# Revit family: reyq22t
name_source: partatom
category: Mechanical Equipment
revit_build: Autodesk Revit 2017 (Build: 20170816_0615(x64)
units: mm (PartAtom-declared; Revit-internal decimal feet)

## family parameters
Cut with Voids When Loaded = No
Host = Face
OmniClass Number = 23.75.10.21.14
OmniClass Title = Rooftop Heat Pumps
Part Type = Normal
Room Calculation Point = No
Round Connector Dimension = Use Diameter
Shared = No

## types (1)
- reyq22t
    COP at max. capacity 6°CWB kW/kW = 4.10 kW/kW
    COP at maximum capacity kW = 0
    COP at nom. capacity 6°CWB kW/kW = 4.29 kW/kW
    COP at nom. capacity Eurovent kW/kW = 0
    COP at nominal capacity kW = 0
    Capacity range HP = 22 HP
    Continuous heating = v
    Cooling capacity Nom. 35°CDB kW = 61.5 (1) kW
    Cooling capacity Nom. Eurovent kW = 0
    Cooling capacity Nom. kW = 0
    Current - 50Hz Maximum fuse amps (MFA) A = 50 A
    Default Elevation = 1000 mm  [stored 3.28084 ft]
    Description = Air cooled - heat recovery
    Dimensions Unit Height/Width/Depth mm = -/-/-
    EER at nom. capacity 35°CDB kW/kW = 3.75 kW/kW
    EER at nom. capacity Eurovent kW/kW = 0
    ESEER - Automatic = 07.lip
    ESEER - Standard = maj.54
    Fan Discharge direction = 0
    Fan External static pressure Max. Pa = 0
    Fan External static pressure Nom. Pa = 0
    Fan Type = 0
    Heating capacity Max. 6°CWB kW = 69.0 (2) kW
    Heating capacity Max. kW = 0
    Heating capacity Nom. 6°CWB kW = 61.5 (2) kW
    Heating capacity Nom. Eurovent kW = 0
    Heating capacity Nom. kW = 0
    IfcExportAs = IfcUnitaryEquipmentType
    IfcExportType = ROOFTOPUNIT
    Indoor index connection Max. = 715
    Indoor index connection Min. = 275
    Indoor index connection Nom. = 550
    Installation Manual = http://www.daikineurope.com
    Manufacturer = Daikin Europe N.V.
    Maximum number of connectable indoor units = 64 (5)
    Model = VRV IV
    Operation range Cooling Min./Max. °CDB = -5.0/43.0 °CDB
    Operation range Heating Min./Max. °CWB = -20/15.5 °CWB
    Operation range Inlet water temperature Cooling Min./Max. °CDB = -/-
    Operation range Inlet water temperature Heating Min./Max. °CWB = -/-
    Piping connections Between Compressor module (CM) and heat exchanger module (HM) Gas OD mm = 0
    Piping connections Between Compressor module (CM) and heat exchanger module (HM) Liquid OD mm = 0
    Piping connections Between Compressor module (CM) and indoor units (IU) Gas OD mm = 0
    Piping connections Between Compressor module (CM) and indoor units (IU) Liquid OD mm = 0
    Piping connections Discharge gas OD mm = 28.6 mm
    Piping connections Gas OD mm = 28.6 mm
    Piping connections Liquid OD mm = 15.9 mm
    Piping connections Oil equalizing OD mm = 0
    Piping connections Total piping length System Actual m = 1,000 (9) m
    Power input - 50Hz Cooling Nom. 35°CDB kW = 16,38 kW
    Power input - 50Hz Cooling Nom. Eurovent kW = 0
    Power input - 50Hz Heating Max. 6°CWB kW = 16,81 kW
    Power input - 50Hz Heating Nom. 6°CWB kW = 14,34 kW
    Power input - 50Hz Heating Nom. Eurovent kW = 0
    Power supply Phase/Frequency/Voltage = 3N~/50/380-415 V
    RSen_C_IFC_version = 2x3
    RSen_C_code_ETIM = Air-conditioning split system – multi-split condensing unit, air-cooled
    RSen_C_code_ETIM_URL = https://prod.etim-international.com
    RSen_C_code_article = REYQ22T7Y1B
    RSen_C_code_product = REYQ22T
    RSen_C_code_product_class = REYQ-T
    RSen_C_content_date_changed = 13/01/2017
    RSen_C_content_date_issue = 13/01/2017
    RSen_C_content_provider = Daikin Europe N.V.
    RSen_C_content_version = v1.0
    RSen_C_description = Air cooled - heat recovery
    RSen_C_diameter_type = OD
    RSen_C_diameter_type_index = 1
    RSen_C_license = Creative Commons Attribution NoDerivs (CC-ND)
    RSen_C_license_info = https://tldrlegal.com
    RSen_C_material = RSen_x_rgb 202 196 176 T00 silk gray_gen
    RSen_C_model = VRV IV
    RSen_C_revit_version = 2015
    RSen_C_type = VRV IV heat recovery
    RSen_C_type_comments = Outdoor unit
    RSen_E_c01_apparent_power = 16810 VA
    RSen_E_c01_apparent_power_phase_1 = 5603 VA
    RSen_E_c01_apparent_power_phase_2 = 5603 VA
    RSen_E_c01_apparent_power_phase_3 = 5603 VA
    RSen_E_c01_current = 0 A
    RSen_E_c01_description = c01_el
    RSen_E_c01_division_engine = No
    RSen_E_c01_load_class = Other
    RSen_E_c01_number_of_poles = 3
    RSen_E_c01_power = 16810 W
    RSen_E_c01_power_factor = 1
    RSen_E_c01_power_factor_state = Lagging
    RSen_E_c01_system_type = Power - Unbalanced
    RSen_E_c01_voltage = 400 V
    RSen_E_c01_yes_no = Yes
    RSen_E_c02_description = c02_controls
    RSen_E_c02_yes_no = Yes
    RSen_P_c01_description = c01_liquid pipe
    RSen_P_c01_diameter = 16 mm  [stored 0.0524934 ft]
    RSen_P_c01_diameter_calc = 16 mm  [stored 0.0524934 ft]
    RSen_P_c01_flow_configuration = Calculated
    RSen_P_c01_flow_direction = Out
    RSen_P_c01_loss_method = Not Defined
    RSen_P_c01_system_classification = Hydronic Supply
    RSen_P_c01_yes_no = Yes
    RSen_P_c02_description = c02_gas pipe
    RSen_P_c02_diameter = 29 mm
    RSen_P_c02_diameter_calc = 29 mm
    RSen_P_c02_flow_configuration = Calculated
    RSen_P_c02_flow_direction = In
    RSen_P_c02_loss_method = Not Defined
    RSen_P_c02_system_classification = Hydronic Return
    RSen_P_c02_yes_no = Yes
    RSen_P_c03_description = c03_equalising pipe
    RSen_P_c03_diameter = 29 mm
    RSen_P_c03_diameter_calc = 29 mm
    RSen_P_c03_flow_configuration = Calculated
    RSen_P_c03_flow_direction = Bidirectional
    RSen_P_c03_loss_method = Not Defined
    RSen_P_c03_system_classification = Global
    RSen_P_c03_yes_no = Yes
    Refrigerant Charge TCO2Eq = 0
    Refrigerant Charge kg = 0
    Refrigerant GWP = 0
    Refrigerant Type = 0
    Sound power level Cooling Nom. dBA = 0
    Sound pressure level Cooling Nom. dBA = 0
    Specification Text = https://my.daikin.eu
    System Compressor unit = 0
    System Function unit = 0
    System Heat exchanger unit = 0
    System Outdoor unit module 1 = REYQ10T
    System Outdoor unit module 2 = REYQ12T
    System Outdoor unit module 3 = 0
    System Outdoor unit module 4 = 0
    TBQ_I BaseKeynote = 58.10
    TBQ_I Spacing_default = 200 mm  [stored 0.656168 ft]
    TBQ_I Spacing_minimum = 20 mm  [stored 0.0656168 ft]
    Type Comments = Outdoor unit
    URL = www.daikineurope.com
    Weight Unit kg = 0
    ZZZ_Clearance behind unit_Length = 600 mm  [stored 1.9685 ft]
    ZZZ_Clearance zone_back_Length = 300 mm  [stored 0.984252 ft]
    ZZZ_Clearance zone_bottom_Length = 0 mm  [stored 0 ft]
    ZZZ_Clearance zone_front_Length = 500 mm  [stored 1.64042 ft]
    ZZZ_Clearance zone_left_Length = 10 mm  [stored 0.0328084 ft]
    ZZZ_Clearance zone_material_Material = RSen_x_rgb 255 128 128 T80 red_gen
    ZZZ_Clearance zone_right_Length = 10 mm  [stored 0.0328084 ft]
    ZZZ_Clearance zone_top_Length = 0 mm  [stored 0 ft]
    ZZZ_Component_01_LOD400_FamilyType_Mechanical Equipment = GEO_none_daikin : standard
    ZZZ_Component_01_Y_Length = 0 mm  [stored 0 ft]
    ZZZ_Component_01_Z_Length = 0 mm  [stored 0 ft]
    ZZZ_Component_01_description_Text = REYQ10T
    ZZZ_Component_01_fan_X_Length = 30 mm  [stored 0.0984252 ft]
    ZZZ_Component_01_fan_Y_Length = 0 mm  [stored 0 ft]
    ZZZ_Component_01_fan_Z_Length = 0 mm  [stored 0 ft]
    ZZZ_Component_01_fan_height_Length = 3 mm  [stored 0.00984252 ft]
    ZZZ_Component_01_fan_length_Length = 830 mm  [stored 2.7231 ft]
    ZZZ_Component_01_fan_material_Material = RSen_x_rgb 189 187 185 T80 gray_gen
    ZZZ_Component_01_fan_plane_Integer = 1
    ZZZ_Component_01_fan_width_Length = 725 mm  [stored 2.37861 ft]
    ZZZ_Component_01_height_Length = 1685 mm  [stored 5.52822 ft]
    ZZZ_Component_01_length_Length = 930 mm  [stored 3.05118 ft]
    ZZZ_Component_01_material_Material = RSen_x_rgb 202 196 176 T00 silk gray_gen
    ZZZ_Component_01_width_Length = 765 mm  [stored 2.50984 ft]
    ZZZ_Component_02_LOD400_FamilyType_Mechanical Equipment = GEO_none_daikin : standard
    ZZZ_Component_02_Y_Length = 0 mm  [stored 0 ft]
    ZZZ_Component_02_Z_Length = 0 mm  [stored 0 ft]
    ZZZ_Component_02_description_Text = REYQ12T
    ZZZ_Component_02_fan_X_Length = 30 mm  [stored 0.0984252 ft]
    ZZZ_Component_02_fan_Y_Length = 0 mm  [stored 0 ft]
    ZZZ_Component_02_fan_Z_Length = 0 mm  [stored 0 ft]
    ZZZ_Component_02_fan_height_Length = 3 mm  [stored 0.00984252 ft]
    ZZZ_Component_02_fan_length_Length = 830 mm  [stored 2.7231 ft]
    ZZZ_Component_02_fan_material_Material = RSen_x_rgb 189 187 185 T80 gray_gen
    ZZZ_Component_02_fan_plane_Integer = 1
    ZZZ_Component_02_fan_width_Length = 725 mm  [stored 2.37861 ft]
    ZZZ_Component_02_height_Length = 1685 mm  [stored 5.52822 ft]
    ZZZ_Component_02_length_Length = 930 mm  [stored 3.05118 ft]
    ZZZ_Component_02_material_Material = RSen_x_rgb 202 196 176 T00 silk gray_gen
    ZZZ_Component_02_width_Length = 765 mm  [stored 2.50984 ft]
    ZZZ_Component_03_LOD400_FamilyType_Mechanical Equipment = GEO_none_daikin : standard
    ZZZ_Component_03_Y_Length = 0 mm  [stored 0 ft]
    ZZZ_Component_03_Z_Length = 0 mm  [stored 0 ft]
    ZZZ_Component_03_description_Text = -
    ZZZ_Component_03_fan_X_Length = 0 mm  [stored 0 ft]
    ZZZ_Component_03_fan_Y_Length = 0 mm  [stored 0 ft]
    ZZZ_Component_03_fan_Z_Length = 0 mm  [stored 0 ft]
    ZZZ_Component_03_fan_height_Length = 0 mm  [stored 0 ft]
    ZZZ_Component_03_fan_length_Length = 0 mm  [stored 0 ft]
    ZZZ_Component_03_fan_material_Material = RSen_x_rgb 189 187 185 T80 gray_gen
    ZZZ_Component_03_fan_plane_Integer = 1
    ZZZ_Component_03_fan_width_Length = 0 mm  [stored 0 ft]
    ZZZ_Component_03_height_Length = 0 mm  [stored 0 ft]
    ZZZ_Component_03_length_Length = 0 mm  [stored 0 ft]
    ZZZ_Component_03_material_Material = RSen_x_rgb 202 196 176 T00 silk gray_gen
    ZZZ_Component_03_width_Length = 0 mm  [stored 0 ft]
    ZZZ_Component_04_LOD400_FamilyType_Mechanical Equipment = GEO_none_daikin : standard
    ZZZ_Component_04_Y_Length = 0 mm  [stored 0 ft]
    ZZZ_Component_04_Z_Length = 0 mm  [stored 0 ft]
    ZZZ_Component_04_description_Text = -
    ZZZ_Component_04_fan_X_Length = 0 mm  [stored 0 ft]
    ZZZ_Component_04_fan_Y_Length = 0 mm  [stored 0 ft]
    ZZZ_Component_04_fan_Z_Length = 0 mm  [stored 0 ft]
    ZZZ_Component_04_fan_height_Length = 0 mm  [stored 0 ft]
    ZZZ_Component_04_fan_length_Length = 0 mm  [stored 0 ft]
    ZZZ_Component_04_fan_material_Material = <By Category>
    ZZZ_Component_04_fan_plane_Integer = 1
    ZZZ_Component_04_fan_width_Length = 0 mm  [stored 0 ft]
    ZZZ_Component_04_height_Length = 0 mm  [stored 0 ft]
    ZZZ_Component_04_length_Length = 0 mm  [stored 0 ft]
    ZZZ_Component_04_material_Material = <By Category>
    ZZZ_Component_04_width_Length = 0 mm  [stored 0 ft]
    ZZZ_Connection zone_back_Length = 0 mm  [stored 0 ft]
    ZZZ_Connection zone_bottom_Length = 0 mm  [stored 0 ft]
    ZZZ_Connection zone_front_Length = 0 mm  [stored 0 ft]
    ZZZ_Connection zone_left_Length = 0 mm  [stored 0 ft]
    ZZZ_Connection zone_material_Material = RSen_x_rgb 255 128 128 T80 red_gen
    ZZZ_Connection zone_right_Length = 0 mm  [stored 0 ft]
    ZZZ_Connection zone_top_Length = 0 mm  [stored 0 ft]
    ZZZ_E_c01_X_Length = 0 mm  [stored 0 ft]
    ZZZ_E_c01_Y_Length = 0 mm  [stored 0 ft]
    ZZZ_E_c01_Z_Length = -300 mm  [stored -0.984252 ft]
    ZZZ_E_c01_plane_Integer = 2
    ZZZ_Housing_medium and coarse_FamilyType_Mechanical Equipment = GEO_medium and coarse_daikin : standard
    ZZZ_Logo_FamilyType_Generic Models = RSen_55_GM_FB_logo outdoor unit - SH_daikin : standard
    ZZZ_Logo_Z_Length = 0 mm  [stored 0 ft]
    ZZZ_Logo_plane_Integer = 3
    ZZZ_Lookup table name_Text = RSen_55_ME_FB_indoor unit - outdoor unit
    ZZZ_Maintenance zone_back_Length = 0 mm  [stored 0 ft]
    ZZZ_Maintenance zone_bottom_Length = 0 mm  [stored 0 ft]
    ZZZ_Maintenance zone_front_Length = 0 mm  [stored 0 ft]
    ZZZ_Maintenance zone_left_Length = 0 mm  [stored 0 ft]
    ZZZ_Maintenance zone_material_Material = RSen_x_rgb 255 128 128 T80 red_gen
    ZZZ_Maintenance zone_right_Length = 0 mm  [stored 0 ft]
    ZZZ_Maintenance zone_top_Length = 0 mm  [stored 0 ft]
    ZZZ_Neighbour unit_offset_back_Length = 300 mm  [stored 0.984252 ft]
    ZZZ_Neighbour unit_offset_front_Length = 500 mm  [stored 1.64042 ft]
    ZZZ_Neighbour unit_offset_left_Length = 10 mm  [stored 0.0328084 ft]
    ZZZ_Neighbour unit_offset_right_Length = 10 mm  [stored 0.0328084 ft]
    ZZZ_Offset_Length = 1000 mm  [stored 3.28084 ft]
    ZZZ_P_c01_X_Length = 365 mm  [stored 1.19751 ft]
    ZZZ_P_c01_Y_Length = -317 mm
    ZZZ_P_c01_Z_Length = -339 mm  [stored -1.1122 ft]
    ZZZ_P_c01_length_Length = 100 mm  [stored 0.328084 ft]
    ZZZ_P_c01_plane_Integer = 2
    ZZZ_P_c02_X_Length = 305 mm  [stored 1.00066 ft]
    ZZZ_P_c02_Y_Length = -277 mm
    ZZZ_P_c02_Z_Length = -195 mm  [stored -0.639764 ft]
    ZZZ_P_c02_length_Length = 100 mm  [stored 0.328084 ft]
    ZZZ_P_c02_plane_Integer = 2
    ZZZ_P_c03_X_Length = 225 mm  [stored 0.738189 ft]
    ZZZ_P_c03_Y_Length = -277 mm
    ZZZ_P_c03_Z_Length = -208 mm
    ZZZ_P_c03_length_Length = 100 mm  [stored 0.328084 ft]
    ZZZ_P_c03_plane_Integer = 2
    ZZZ_Placement zone_material_Material = RSen_x_rgb 255 128 128 T80 red_gen
    ZZZ_Visualized connectors_FamilyType_Generic Models = RSen_55_GM_FB_none_daikin : standard
    ZZZ_Zones_plane_Integer = 2

note: [stored X ft] marks values corroborated as IEEE doubles in the binary element streams (Revit-internal decimal feet)

## geometry (parser evidence)
native form markers: Blend x4, Sweep x33
no freeform markers — native parametric forms only
